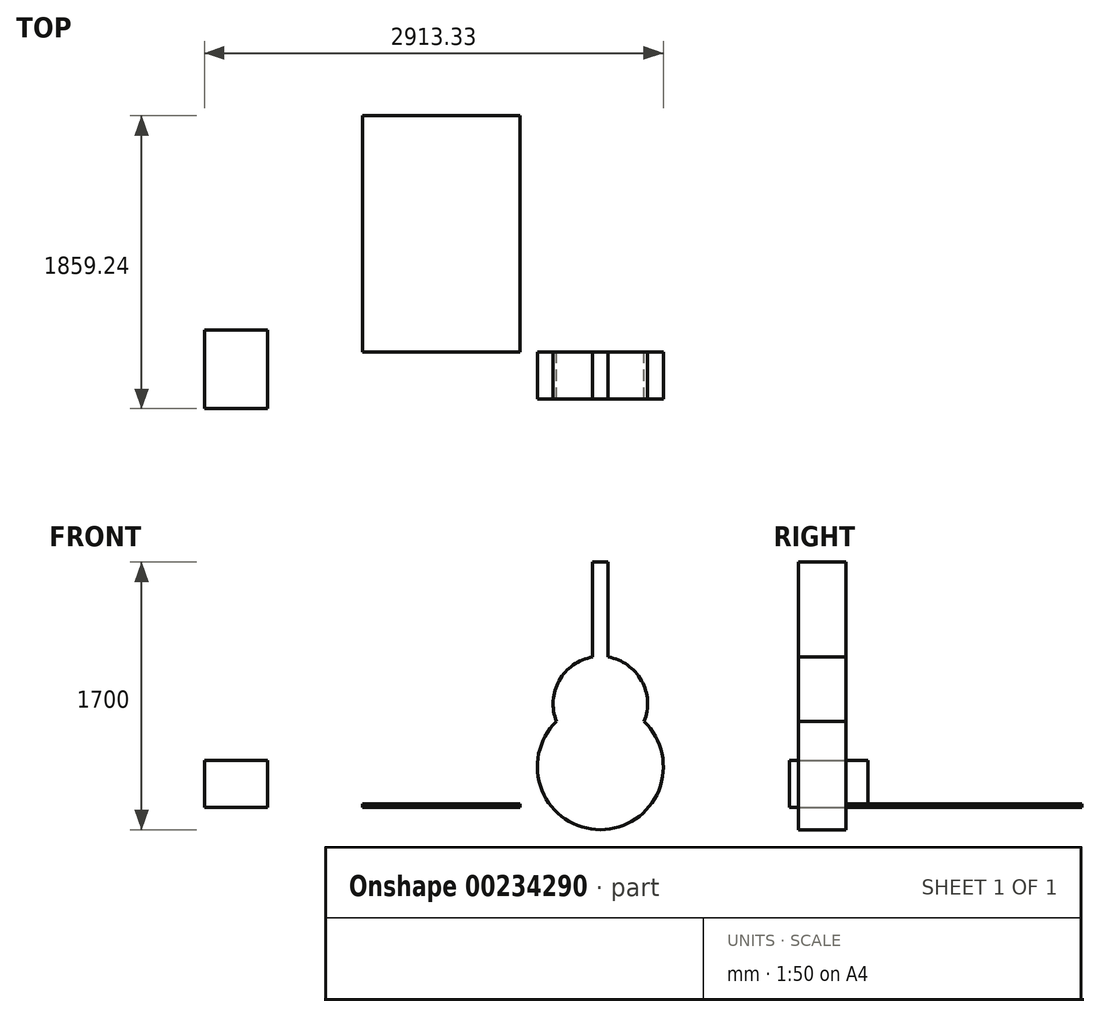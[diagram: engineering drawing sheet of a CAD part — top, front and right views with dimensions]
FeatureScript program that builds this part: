
annotation { "Feature Type Name" : "Feature", "Feature Type Description" : "" }
export const myFeature = defineFeature(function(context is Context, id is Id, definition is map)
    precondition{}
    {
        {
            var Q0;
            Q0=qCreatedBy(makeId("Top.planeOp"),FACE);
            var sketch = newSketch(context, id + "F0", { "sketchPlane" : qUnion([Q0])});
            skLineSegment(sketch, "E0.bottom", {"start": v(0, 0) * mm, "end": v(1000, 0) * mm});
            skLineSegment(sketch, "E0.top", {"start": v(0, 1500) * mm, "end": v(1000, 1500) * mm});
            skLineSegment(sketch, "E0.left", {"start": v(0, 0) * mm, "end": v(0, 1500) * mm});
            skLineSegment(sketch, "E0.right", {"start": v(1000, 0) * mm, "end": v(1000, 1500) * mm});
            skSolve(sketch);
        }
        {
            var Q0;
            Q0=qCreatedBy(makeId("Front.planeOp"),FACE);
            var sketch = newSketch(context, id + "F5", { "sketchPlane" : qUnion([Q0])});
            skCircle(sketch, "E1", {"center": v(1511.47, 259.66) * mm, "radius": 400 * mm});
            skCircle(sketch, "E2", {"center": v(1511.47, 659.66) * mm, "radius": 300 * mm});
            skLineSegment(sketch, "E3.bottom", {"start": v(1461.47, 1559.66) * mm, "end": v(1561.47, 1559.66) * mm});
            skLineSegment(sketch, "E3.top", {"start": v(1461.47, 955.46) * mm, "end": v(1561.47, 955.46) * mm});
            skLineSegment(sketch, "E3.left", {"start": v(1461.47, 1559.66) * mm, "end": v(1461.47, 955.46) * mm});
            skLineSegment(sketch, "E3.right", {"start": v(1561.47, 1559.66) * mm, "end": v(1561.47, 955.46) * mm});
            skLineSegment(sketch, "E4", {"start": v(1461.47, 1559.66) * mm, "end": v(1561.47, 955.46) * mm, "construction": true});
            skPoint(sketch, "E5", {"position": v(1511.47, 1257.56) * mm});
            skSolve(sketch);
        }
        {
            var Q0;
            {var subQ0=sQuery(id+"F5.wireOp",EDGE,"E2");var subQ1=sQuery(id+"F5.wireOp",EDGE,"E1");var subQ2=makeQuery(id+"F5.imprint","INTERSECT",VERTEX,{"disambiguationData":[OD(0.0)],"derivedFrom":[subQ1,subQ0]});Q0=makeQuery(id+"F5.imprint","IMPRINT",FACE,{"disambiguationData":[TD([[makeQuery(id+"F5.imprint","IMPRINT",EDGE,{"disambiguationData":[TD([[subQ2,-1.0]])],"derivedFrom":subQ1}),1.0]])]});}
            var Q1;
            {var subQ4=sQuery(id+"F5.wireOp",EDGE,"E3.top");Q1=makeQuery(id+"F5.imprint","IMPRINT",FACE,{"disambiguationData":[TD([[makeQuery(id+"F5.imprint","IMPRINT",EDGE,{"derivedFrom":subQ4}),-1.0]])]});}
            var Q2;
            {var subQ0=sQuery(id+"F5.wireOp",EDGE,"E2");var subQ1=sQuery(id+"F5.wireOp",EDGE,"E1");var subQ2=makeQuery(id+"F5.imprint","INTERSECT",VERTEX,{"disambiguationData":[OD(0.0)],"derivedFrom":[subQ1,subQ0]});Q2=makeQuery(id+"F5.imprint","IMPRINT",FACE,{"disambiguationData":[TD([[makeQuery(id+"F5.imprint","IMPRINT",EDGE,{"disambiguationData":[TD([[subQ2,1.0]])],"derivedFrom":subQ1}),1.0]])]});}
            var Q3;
            {var subQ0=sQuery(id+"F5.wireOp",EDGE,"E3.top");Q3=makeQuery(id+"F5.imprint","IMPRINT",FACE,{"disambiguationData":[TD([[makeQuery(id+"F5.imprint","IMPRINT",EDGE,{"derivedFrom":subQ0}),1.0]])]});}
            var Q4;
            Q4=makeQuery(id+"F5.imprint","IMPRINT",FACE,{"disambiguationData":[TD([[makeQuery(id+"F5.imprint","IMPRINT",EDGE,{"derivedFrom":sQuery(id+"F5.wireOp",EDGE,"E3.bottom")}),-1.0]])]});
            extrude(context, id + "F1", {"entities" : qUnion([Q0, Q1, Q2, Q3, Q4]), "depth" : 300 * mm});
        }
        {
            var Q0;
            Q0=qCreatedBy(makeId("Top.planeOp"),FACE);
            var sketch = newSketch(context, id + "F2", { "sketchPlane" : qUnion([Q0])});
            skLineSegment(sketch, "E6.bottom", {"start": v(-1001.86, -359.24) * mm, "end": v(-601.86, -359.24) * mm});
            skLineSegment(sketch, "E6.top", {"start": v(-1001.86, 140.76) * mm, "end": v(-601.86, 140.76) * mm});
            skLineSegment(sketch, "E6.left", {"start": v(-1001.86, -359.24) * mm, "end": v(-1001.86, 140.76) * mm});
            skLineSegment(sketch, "E6.right", {"start": v(-601.86, -359.24) * mm, "end": v(-601.86, 140.76) * mm});
            skSolve(sketch);
        }
        {
            var Q0;
            Q0=makeQuery(id+"F2.imprint","IMPRINT",FACE,{"disambiguationData":[TD([[makeQuery(id+"F2.imprint","IMPRINT",EDGE,{"derivedFrom":sQuery(id+"F2.wireOp",EDGE,"E6.bottom")}),1.0]])]});
            extrude(context, id + "F3", {"entities" : qUnion([Q0]), "depth" : 300 * mm});
        }
        {
            var Q0;
            Q0=makeQuery(id+"F0.imprint","IMPRINT",FACE,{"disambiguationData":[TD([[makeQuery(id+"F0.imprint","IMPRINT",EDGE,{"derivedFrom":sQuery(id+"F0.wireOp",EDGE,"E0.bottom")}),1.0]])]});
            extrude(context, id + "F4", {"entities" : qUnion([Q0]), "depth" : 25 * mm});
        }
    });
